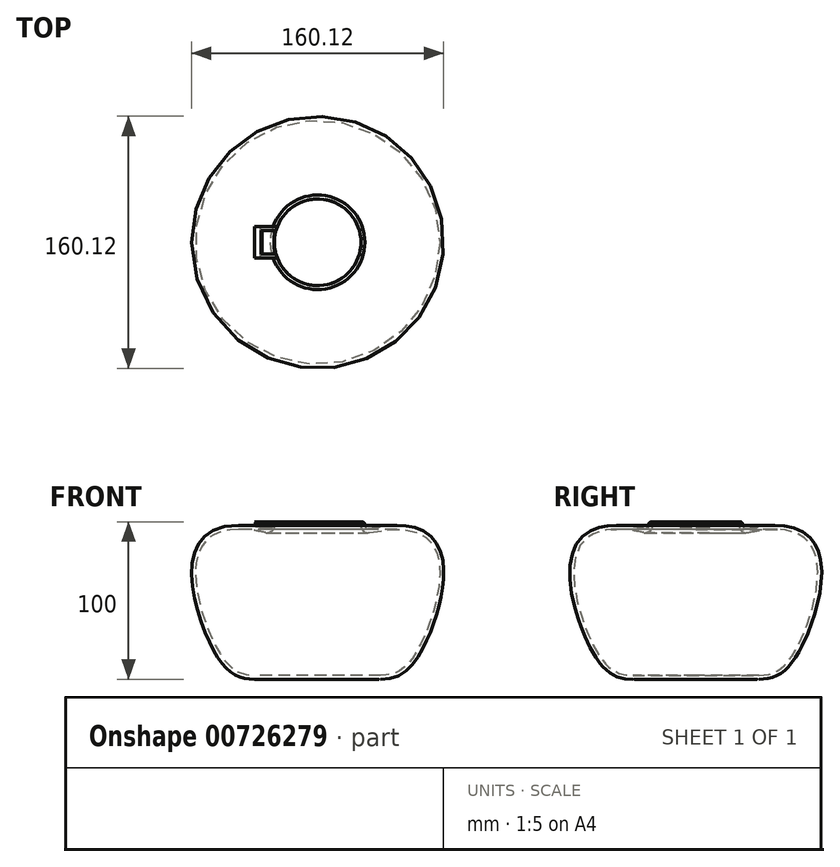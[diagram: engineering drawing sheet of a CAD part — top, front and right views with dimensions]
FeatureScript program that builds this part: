
annotation { "Feature Type Name" : "Feature", "Feature Type Description" : "" }
export const myFeature = defineFeature(function(context is Context, id is Id, definition is map)
    precondition{}
    {
        {
            var Q0;
            Q0=qCreatedBy(makeId("Front.planeOp"),FACE);
            var sketch = newSketch(context, id + "F0", { "sketchPlane" : qUnion([Q0])});
            skLineSegment(sketch, "E0", {"start": v(40, 0) * mm, "end": v(0, 0) * mm});
            skLineSegment(sketch, "E1", {"start": v(0, 0) * mm, "end": v(0, 100) * mm});
            skLineSegment(sketch, "E2", {"start": v(0, 100) * mm, "end": v(30, 100) * mm});
            skLineSegment(sketch, "E3", {"start": v(30, 100) * mm, "end": v(30, 95) * mm});
            skFitSpline(sketch, "E4", {"points": [v(30, 95) * mm, v(68.8, 23.7) * mm, v(40, 0) * mm], "startDerivative": vector(335.19, 82.32) * mm, "endDerivative": vector(-85.75, 0) * mm});
            skSolve(sketch);
        }
        {
            var Q0;
            Q0 = qSketchRegion(id + "F0", true);
            var Q1;
            Q1=sQuery(id+"F0.wireOp",EDGE,"E1");
            revolve(context, id + "F1", {"surfaceOperationType" : NewSurfaceOperationType.NEW, "entities" : qUnion([Q0]), "axis" : qUnion([Q1]), "revolveType" : RevolveType.FULL});
        }
        {
            var Q0;
            Q0=makeQuery(id+"F1.opRevolve","SWEPT_FACE",FACE,{"disambiguationData":[OSD([sQuery(id+"F0.wireOp",EDGE,"E2")])]});
            var sketch = newSketch(context, id + "F2", { "sketchPlane" : qUnion([Q0])});
            skLineSegment(sketch, "E5", {"start": v(0, 0) * mm, "end": v(0, -10) * mm});
            skLineSegment(sketch, "E6", {"start": v(0, -10) * mm, "end": v(-40, -10) * mm});
            skLineSegment(sketch, "E7", {"start": v(-40, -10) * mm, "end": v(-40, 10) * mm});
            skLineSegment(sketch, "E8", {"start": v(-40, 10) * mm, "end": v(0, 10) * mm});
            skLineSegment(sketch, "E9", {"start": v(0, 10) * mm, "end": v(0, 0) * mm});
            skSolve(sketch);
        }
        {
            var Q0;
            Q0=qCreatedBy(makeId("Front.planeOp"),FACE);
            var sketch = newSketch(context, id + "F3", { "sketchPlane" : qUnion([Q0])});
            skLineSegment(sketch, "E10", {"start": v(0, 100) * mm, "end": v(3.83, 96.79) * mm});
            skSolve(sketch);
        }
        {
            var Q0;
            {var subQ0=sQuery(id+"F2.wireOp",EDGE,"E7");Q0=makeQuery(id+"F2.imprint","IMPRINT",FACE,{"disambiguationData":[TD([[makeQuery(id+"F2.imprint","IMPRINT",EDGE,{"derivedFrom":subQ0}),-1.0]])]});}
            var Q1;
            Q1=sQuery(id+"F3.wireOp",EDGE,"E10");
            sweep(context, id + "F4", {"operationType" : NewBodyOperationType.ADD, "profiles" : qUnion([Q0]), "path" : qUnion([Q1])});
        }
        {
            var Q0;
            Q0=makeQuery(id+"F1.opRevolve","SWEPT_EDGE",EDGE,{"disambiguationData":[OSD([sQuery(id+"F0.wireOp",EDGE,"E2"),sQuery(id+"F0.wireOp",EDGE,"E3")])]});
            var Q1;
            Q1=makeQuery(id+"F1.opRevolve","SWEPT_EDGE",EDGE,{"disambiguationData":[OSD([sQuery(id+"F0.wireOp",EDGE,"E3"),sQuery(id+"F0.wireOp",EDGE,"E4")])]});
            fillet(context, id + "F5", {"entities" : qUnion([Q0, Q1]), "radius" : 2 * mm, "tangentPropagation" : true, "allowEdgeOverflow" : false});
        }
        {
            var Q0;
            {var subQ0=sQuery(id+"F0.wireOp",EDGE,"E2");Q0=makeQuery(id+"F4.boolean.opBoolean","MERGE",FACE,{"derivedFrom":[makeQuery(id+"F1.opRevolve","SWEPT_FACE",FACE,{"disambiguationData":[OSD([subQ0])]}),makeQuery(id+"F4.opSweep","CAP_FACE",FACE,{"disambiguationData":[OSD([subQ0,sQuery(id+"F0.wireOp",EDGE,"E3"),sQuery(id+"F2.wireOp",EDGE,"E6"),sQuery(id+"F2.wireOp",EDGE,"E7"),sQuery(id+"F2.wireOp",EDGE,"E8"),sQuery(id+"F3.wireOp",VERTEX,"E10.start")])],"isStart":true})]});}
            shell(context, id + "F6", {"entities" : qUnion([Q0]), "thickness" : 2.5 * mm});
        }
    });
